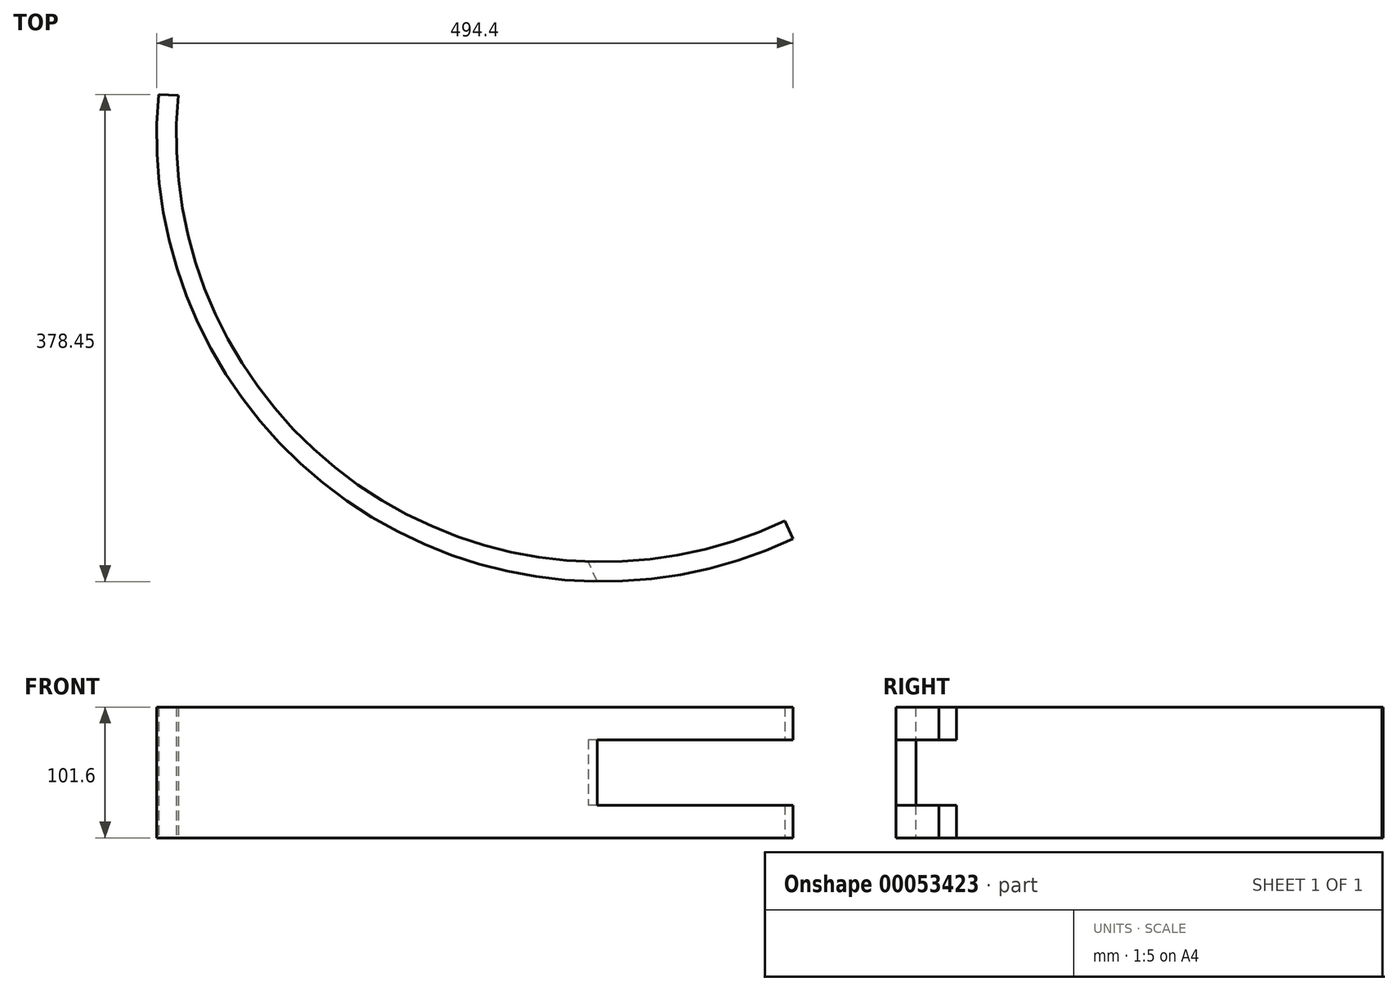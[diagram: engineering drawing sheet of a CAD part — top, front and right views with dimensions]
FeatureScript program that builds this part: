
annotation { "Feature Type Name" : "Feature", "Feature Type Description" : "" }
export const myFeature = defineFeature(function(context is Context, id is Id, definition is map)
    precondition{}
    {
        {
            var Q0;
            Q0=qCreatedBy(makeId("Top.planeOp"),FACE);
            var sketch = newSketch(context, id + "F0", { "sketchPlane" : qUnion([Q0])});
            skArc(sketch, "E0", {"start": v(0.03, 304.8) * mm, "mid": v(139.58, 2.42) * mm, "end": v(471.42, -25.71) * mm});
            skArc(sketch, "E1.0", {"start": v(-15.2, 305.62) * mm, "mid": v(130.97, -10.16) * mm, "end": v(477.7, -39.6) * mm});
            skLineSegment(sketch, "E2", {"start": v(471.42, -25.71) * mm, "end": v(477.7, -39.6) * mm});
            skLineSegment(sketch, "E3", {"start": v(-15.2, 305.62) * mm, "end": v(0.03, 304.8) * mm});
            skLineSegment(sketch, "E4", {"start": v(254.87, -101.88) * mm, "end": v(257.4, -107.84) * mm});
            skLineSegment(sketch, "E5", {"start": v(-147.23, 194.8) * mm, "end": v(-140.86, 194.8) * mm});
            skLineSegment(sketch, "E6", {"start": v(457.9, -31.75) * mm, "end": v(396.62, 114.16) * mm, "construction": true});
            skSolve(sketch);
        }
        {
            var Q0;
            Q0=makeQuery(id+"F0.imprint","IMPRINT",FACE,{"disambiguationData":[TD([[makeQuery(id+"F0.imprint","IMPRINT",EDGE,{"derivedFrom":sQuery(id+"F0.wireOp",EDGE,"E0")}),-1.0]])]});
            extrude(context, id + "F1", {"entities" : qUnion([Q0]), "depth" : 101.6 * mm});
        }
        {
            var Q0;
            Q0=makeQuery(id+"F1.opExtrude","SWEPT_FACE",FACE,{"disambiguationData":[OSD([sQuery(id+"F0.wireOp",EDGE,"E2")])]});
            var sketch = newSketch(context, id + "F2", { "sketchPlane" : qUnion([Q0])});
            skLineSegment(sketch, "E7.bottom", {"start": v(-316.85, 76.2) * mm, "end": v(-139.05, 76.2) * mm});
            skLineSegment(sketch, "E7.top", {"start": v(-316.85, 25.4) * mm, "end": v(-139.05, 25.4) * mm});
            skLineSegment(sketch, "E7.left", {"start": v(-316.85, 76.2) * mm, "end": v(-316.85, 25.4) * mm});
            skLineSegment(sketch, "E7.right", {"start": v(-139.05, 76.2) * mm, "end": v(-139.05, 25.4) * mm});
            skLineSegment(sketch, "E8", {"start": v(-232.98, 0) * mm, "end": v(-232.98, 25.4) * mm});
            skSolve(sketch);
        }
        {
            var Q0;
            Q0 = qSketchRegion(id + "F2", true);
            extrude(context, id + "F3", {"entities" : qUnion([Q0]), "operationType" : NewBodyOperationType.REMOVE, "oppositeDirection" : true, "depth" : 152.4 * mm});
        }
    });
